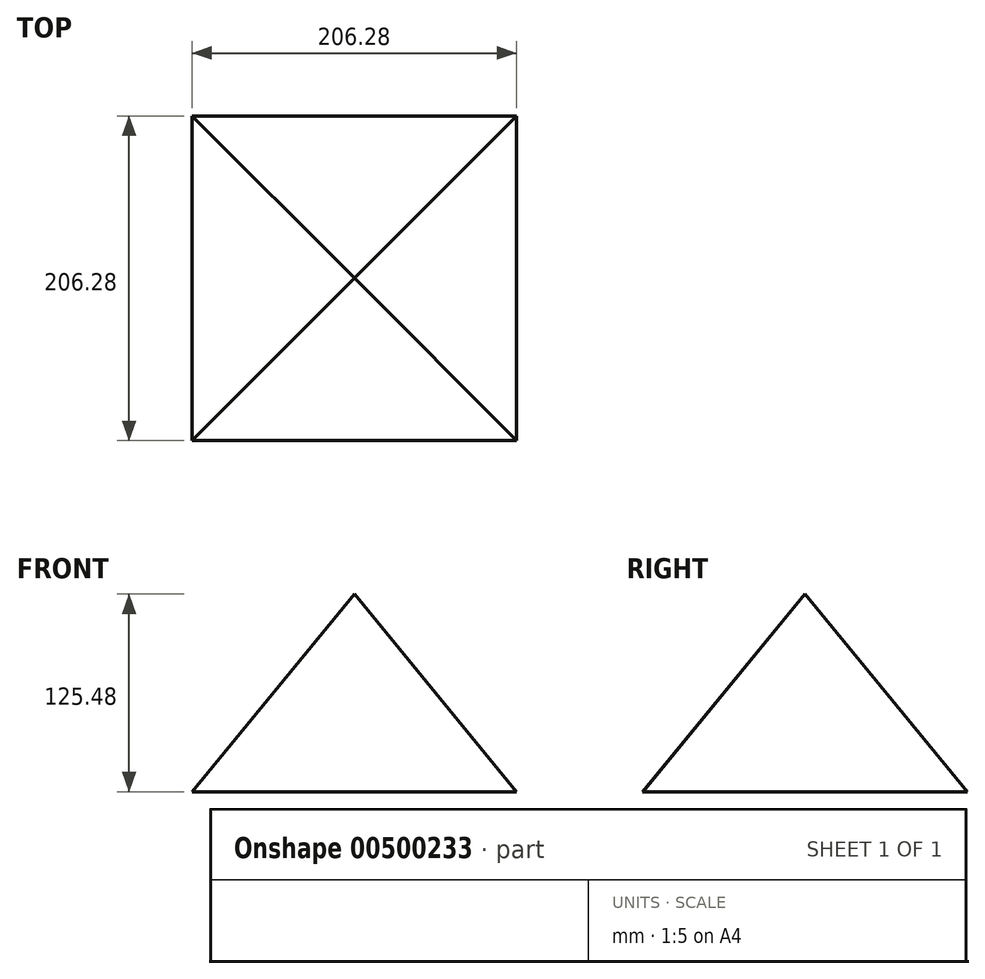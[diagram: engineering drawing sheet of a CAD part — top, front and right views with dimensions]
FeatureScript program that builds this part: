
annotation { "Feature Type Name" : "Feature", "Feature Type Description" : "" }
export const myFeature = defineFeature(function(context is Context, id is Id, definition is map)
    precondition{}
    {
        {
            var Q0;
            Q0=qCreatedBy(makeId("Top.planeOp"),FACE);
            var sketch = newSketch(context, id + "F0", { "sketchPlane" : qUnion([Q0])});
            skCircle(sketch, "E0.cCircle", {"center": v(0, 0) * mm, "radius": 145.82 * mm, "construction": true});
            skLineSegment(sketch, "E0.0", {"start": v(103.14, -103.09) * mm, "end": v(-103.09, -103.14) * mm});
            skLineSegment(sketch, "E0.1", {"start": v(-103.09, -103.14) * mm, "end": v(-103.14, 103.09) * mm});
            skLineSegment(sketch, "E0.2", {"start": v(-103.14, 103.09) * mm, "end": v(103.09, 103.14) * mm});
            skLineSegment(sketch, "E0.3", {"start": v(103.09, 103.14) * mm, "end": v(103.14, -103.09) * mm});
            skSolve(sketch);
        }
        {
            var Q0;
            Q0=qCreatedBy(makeId("Top.planeOp"),FACE);
            cPlane(context, id + "F1", {"entities" : qUnion([Q0]), "cplaneType" : CPlaneType.OFFSET, "offset" : 125.48 * mm, "width" : 152.4 * mm, "height" : 152.4 * mm});
        }
        {
            var Q0;
            Q0=qCreatedBy(id+"F1.planeOp",FACE);
            var sketch = newSketch(context, id + "F2", { "sketchPlane" : qUnion([Q0])});
            skPoint(sketch, "E1", {"position": v(0, 0) * mm});
            skSolve(sketch);
        }
        {
            var Q0;
            Q0=sQuery(id+"F2.wireOp",VERTEX,"E1");
            var Q1;
            Q1=makeQuery(id+"F0.imprint","IMPRINT",FACE,{"disambiguationData":[TD([[makeQuery(id+"F0.imprint","IMPRINT",EDGE,{"derivedFrom":sQuery(id+"F0.wireOp",EDGE,"E0.0")}),-1.0]])]});
            loft(context, id + "F3", {"sheetProfilesArray" : [{ "sheetProfileEntities" : qUnion([Q0]) }, { "sheetProfileEntities" : qUnion([Q1]) }]});
        }
    });
